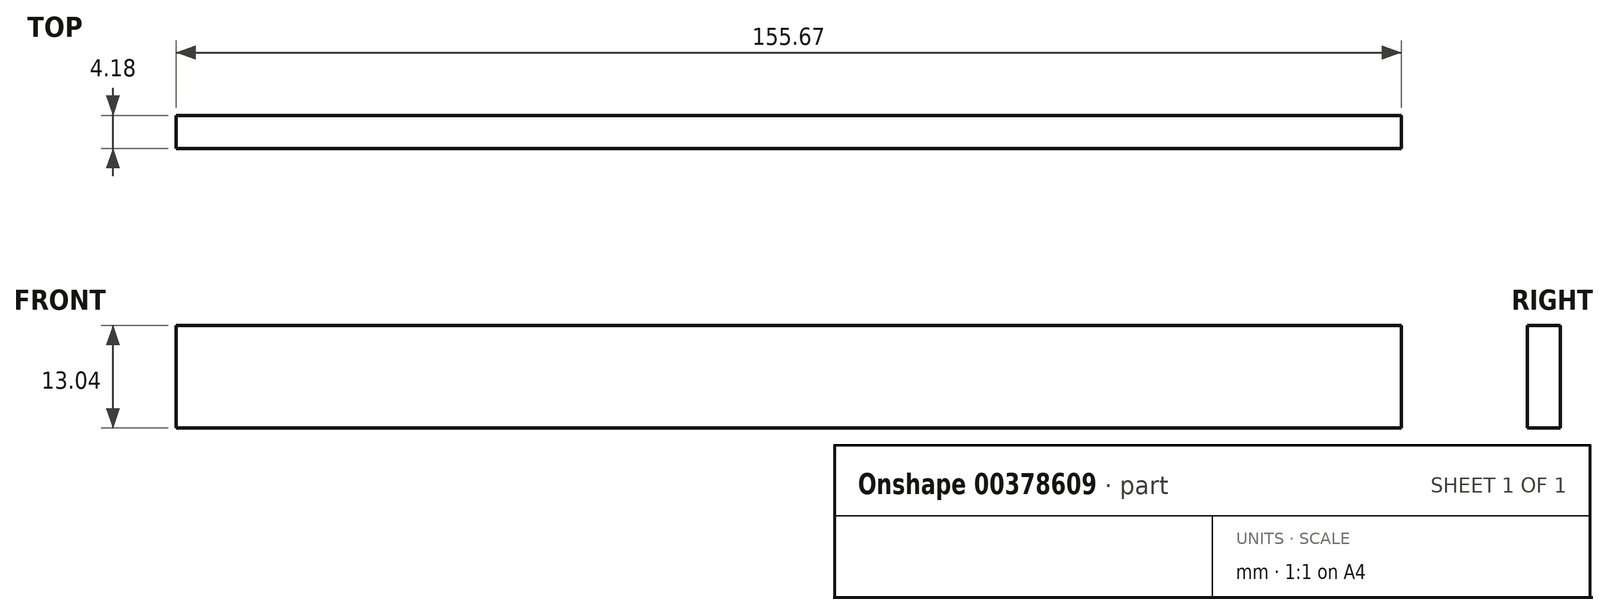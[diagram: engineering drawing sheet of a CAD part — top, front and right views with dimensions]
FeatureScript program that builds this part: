
annotation { "Feature Type Name" : "Feature", "Feature Type Description" : "" }
export const myFeature = defineFeature(function(context is Context, id is Id, definition is map)
    precondition{}
    {
        {
            var Q0;
            Q0=qCreatedBy(makeId("Front.planeOp"),FACE);
            var sketch = newSketch(context, id + "F0", { "sketchPlane" : qUnion([Q0])});
            skLineSegment(sketch, "E0.bottom", {"start": v(0, 0) * mm, "end": v(155.67, 0) * mm});
            skLineSegment(sketch, "E0.top", {"start": v(0, 13.04) * mm, "end": v(155.67, 13.04) * mm});
            skLineSegment(sketch, "E0.left", {"start": v(0, 0) * mm, "end": v(0, 13.04) * mm});
            skLineSegment(sketch, "E0.right", {"start": v(155.67, 0) * mm, "end": v(155.67, 13.04) * mm});
            skSolve(sketch);
        }
        {
            var Q0;
            Q0=makeQuery(id+"F0.imprint","IMPRINT",FACE,{"disambiguationData":[TD([[makeQuery(id+"F0.imprint","IMPRINT",EDGE,{"derivedFrom":sQuery(id+"F0.wireOp",EDGE,"E0.bottom")}),1.0]])]});
            extrude(context, id + "F1", {"entities" : qUnion([Q0]), "oppositeDirection" : true, "depth" : 4.18 * mm});
        }
    });
